# Revit family: Sanitary_Toilets_DURAVIT_Starck-3-wall-mounted-toilet-252709_
name_source: partatom
category: Plumbing Fixtures
revit_build: Autodesk Revit 2015 (Build: 20140903_1530(x64)
units: mm (PartAtom-declared; Revit-internal decimal feet)

## types (1)
- Default
    BIMobject category = Toilets
    BIMobject category code = sanitary-toilets
    BIMobject main category = Sanitary
    BIMobject main category code = sanitary
    Brand url = http://www.duravit.com
    Edition number = 1
    GTIN code = 4021534984808
    IFC Classification = Sanitary Terminal
    Installation instructions = http://pro.duravit.com
    Manufacturer name = DURAVIT
    Masterformat 2014 Code = 01 52 19
    Masterformat 2014 Description = Sanitary Facilities
    Material main = Ceramics
    NBS Reference Code = 35-65-90
    NBS Reference Description = Toilet Systems
    OmniClass Code = 23-31 19 00
    OmniClass Description = Toilets
    Product Guid = 1705f2fd-75c3-4a98-ba40-5427de26389a
    Product SKU = starck-3-wall-mounted-toilet-252709
    Product certification = http://pro.duravit.com
    Product data url = https://bimobject.com
    Product family = Starck 3
    Product group = toilet
    Product name = Starck 3 wall-mounted toilet 252709
    Product url = http://pro.duravit.com
    QR code = http://bimobject.com
    Technical description = http://pro.duravit.com
    UNSPSC Code = 301815
    Uniclass 1.4 Code = L7216
    Uniclass 1.4 Description = Toilets
    Uniclass 2.0 Code = SS-35-65-90
    Uniclass 2.0 Description = Toilet Systems
    Uniclass 2015 Code = Pr_40_20_93
    Uniclass 2015 Name = Urinal and WC fittings
    Uniformat II Code = D2030
    Uniformat II Description = Sanitary Waste
    Youtube clip = http://pro.duravit.com

## geometry (parser evidence)
native form markers: Sweep x4
no freeform markers — native parametric forms only
